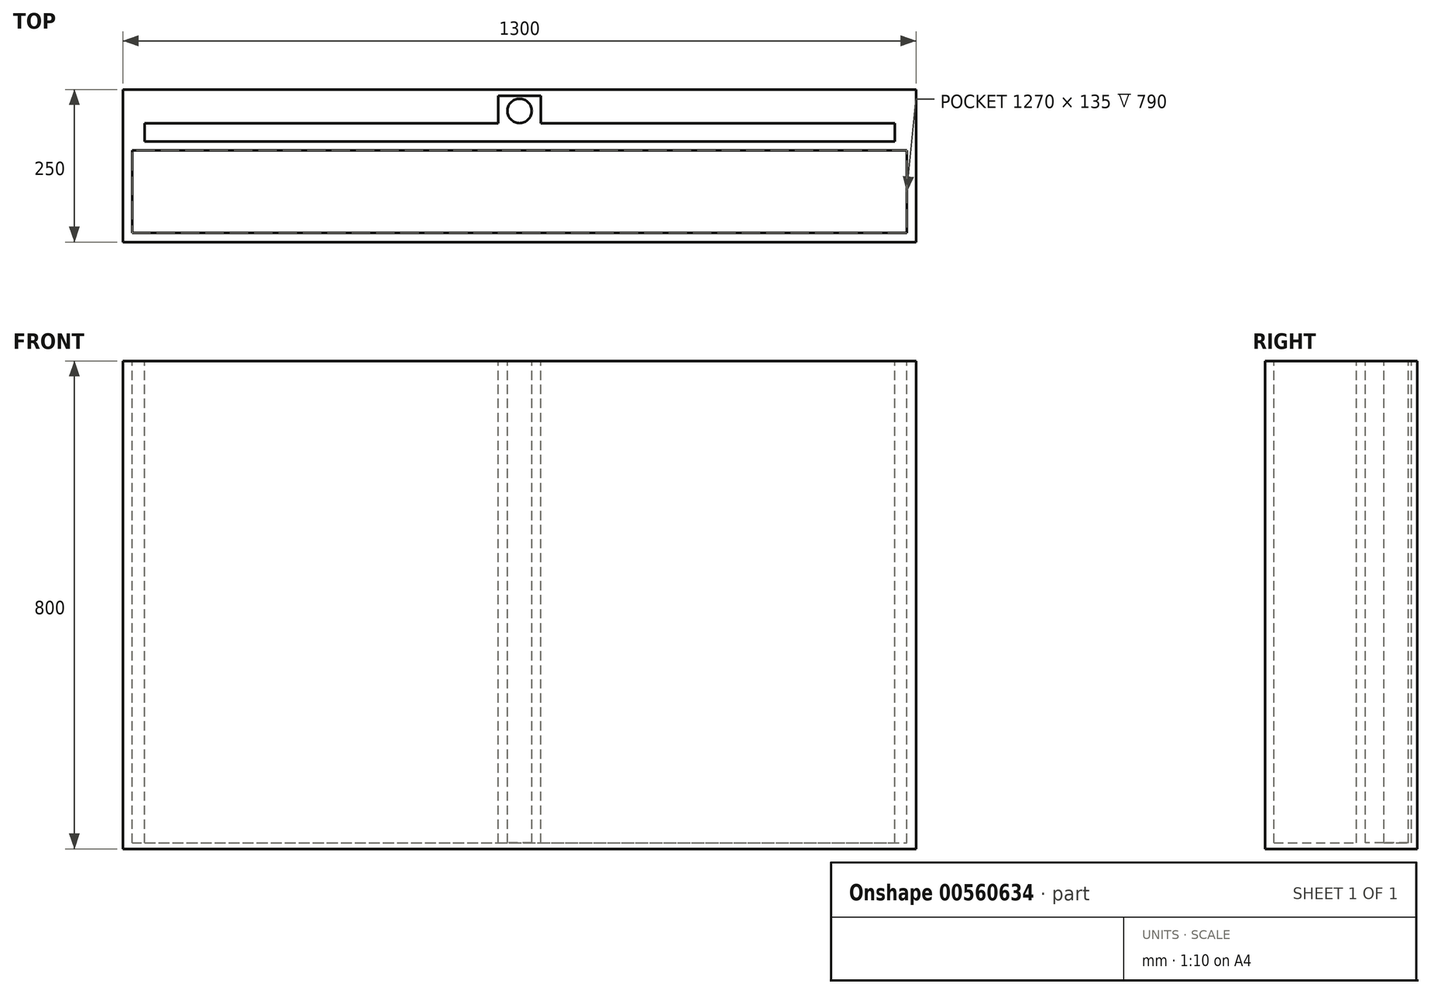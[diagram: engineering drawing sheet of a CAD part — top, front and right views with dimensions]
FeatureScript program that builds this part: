
annotation { "Feature Type Name" : "Feature", "Feature Type Description" : "" }
export const myFeature = defineFeature(function(context is Context, id is Id, definition is map)
    precondition{}
    {
        {
            var Q0;
            Q0=qCreatedBy(makeId("Front.planeOp"),FACE);
            var sketch = newSketch(context, id + "F0", { "sketchPlane" : qUnion([Q0])});
            skLineSegment(sketch, "E0.bottom", {"start": v(0, 0) * mm, "end": v(1300, 0) * mm});
            skLineSegment(sketch, "E0.top", {"start": v(0, -800) * mm, "end": v(1300, -800) * mm});
            skLineSegment(sketch, "E0.left", {"start": v(0, 0) * mm, "end": v(0, -800) * mm});
            skLineSegment(sketch, "E0.right", {"start": v(1300, 0) * mm, "end": v(1300, -800) * mm});
            skSolve(sketch);
        }
        {
            var Q0;
            Q0=makeQuery(id+"F0.imprint","IMPRINT",FACE,{"disambiguationData":[TD([[makeQuery(id+"F0.imprint","IMPRINT",EDGE,{"derivedFrom":sQuery(id+"F0.wireOp",EDGE,"E0.bottom")}),-1.0]])]});
            extrude(context, id + "F1", {"entities" : qUnion([Q0]), "depth" : 250 * mm, "offsetDistance" : 25 * mm});
        }
        {
            var Q0;
            Q0=makeQuery(id+"F1.opExtrude","SWEPT_FACE",FACE,{"disambiguationData":[OSD([sQuery(id+"F0.wireOp",EDGE,"E0.bottom")])]});
            var sketch = newSketch(context, id + "F2", { "sketchPlane" : qUnion([Q0])});
            skLineSegment(sketch, "E1.bottom", {"start": v(35, -10) * mm, "end": v(1265, -10) * mm});
            skLineSegment(sketch, "E1.top", {"start": v(35, -85) * mm, "end": v(1265, -85) * mm});
            skLineSegment(sketch, "E1.left", {"start": v(35, -10) * mm, "end": v(35, -85) * mm});
            skLineSegment(sketch, "E1.right", {"start": v(1265, -10) * mm, "end": v(1265, -85) * mm});
            skCircle(sketch, "E2", {"center": v(650, -35) * mm, "radius": 25 * mm});
            skLineSegment(sketch, "E3", {"start": v(675, -10) * mm, "end": v(675, -35) * mm});
            skLineSegment(sketch, "E4", {"start": v(625, -10) * mm, "end": v(625, -35) * mm});
            skCircle(sketch, "E5", {"center": v(650, -35) * mm, "radius": 20 * mm});
            skLineSegment(sketch, "E6", {"start": v(35, -55) * mm, "end": v(615, -55) * mm});
            skLineSegment(sketch, "E7", {"start": v(615, -55) * mm, "end": v(615, -10) * mm});
            skLineSegment(sketch, "E8", {"start": v(685, -10) * mm, "end": v(685, -55) * mm});
            skLineSegment(sketch, "E9", {"start": v(685, -55) * mm, "end": v(1265, -55) * mm});
            skLineSegment(sketch, "E10.bottom", {"start": v(15, -235) * mm, "end": v(1285, -235) * mm});
            skLineSegment(sketch, "E10.top", {"start": v(15, -100) * mm, "end": v(1285, -100) * mm});
            skLineSegment(sketch, "E10.left", {"start": v(15, -235) * mm, "end": v(15, -100) * mm});
            skLineSegment(sketch, "E10.right", {"start": v(1285, -235) * mm, "end": v(1285, -100) * mm});
            skSolve(sketch);
        }
        {
            var Q0;
            Q0=makeQuery(id+"F2.imprint","IMPRINT",FACE,{"disambiguationData":[TD([[makeQuery(id+"F2.imprint","IMPRINT",EDGE,{"derivedFrom":sQuery(id+"F2.wireOp",EDGE,"E2")}),1.0]])]});
            var Q1;
            Q1=makeQuery(id+"F2.imprint","IMPRINT",FACE,{"disambiguationData":[TD([[makeQuery(id+"F2.imprint","IMPRINT",EDGE,{"derivedFrom":sQuery(id+"F2.wireOp",EDGE,"E1.top")}),1.0]])]});
            var Q2;
            {var subQ0=sQuery(id+"F2.wireOp",EDGE,"E3");Q2=makeQuery(id+"F2.imprint","IMPRINT",FACE,{"disambiguationData":[TD([[makeQuery(id+"F2.imprint","IMPRINT",EDGE,{"derivedFrom":subQ0}),-1.0]])]});}
            var Q3;
            {var subQ0=sQuery(id+"F2.wireOp",EDGE,"E4");Q3=makeQuery(id+"F2.imprint","IMPRINT",FACE,{"disambiguationData":[TD([[makeQuery(id+"F2.imprint","IMPRINT",EDGE,{"derivedFrom":subQ0}),1.0]])]});}
            var Q4;
            Q4=makeQuery(id+"F2.imprint","IMPRINT",FACE,{"disambiguationData":[TD([[makeQuery(id+"F2.imprint","IMPRINT",EDGE,{"derivedFrom":sQuery(id+"F2.wireOp",EDGE,"E10.bottom")}),1.0]])]});
            extrude(context, id + "F3", {"entities" : qUnion([Q0, Q1, Q2, Q3, Q4]), "operationType" : NewBodyOperationType.REMOVE, "oppositeDirection" : true, "depth" : 790 * mm, "offsetDistance" : 25 * mm});
        }
    });
